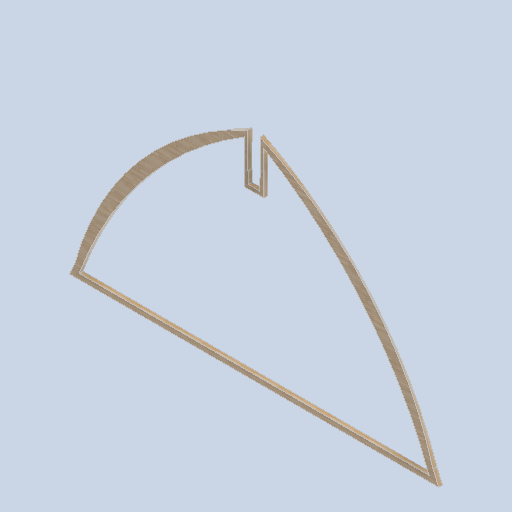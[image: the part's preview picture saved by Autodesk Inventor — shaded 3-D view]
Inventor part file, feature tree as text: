
AUTODESK INVENTOR PART (.ipt)
format: ipt  version: 2024.2 (Build 282272000, 272)  size: 168,448 bytes
history: native  units: in
note: dims shown in document units (in); Inventor stores cm internally (conversion verified against a paired STEP export)
features: other x3, sketch x2, plane x2
ambient origin geometry x8: Origin, YZ Plane, XZ Plane, XY Plane, X Axis, Y Axis, Z Axis, Center Point
bodies: Solid1 (feature_tree)
feature tree (7):
  other  "curve_front_wall_frame.ipt"
  other  "Solid1::curve_front_wall_frame.ipt"
  other  "TaggingFeature1"
  sketch  "Sketch1"  dims[d0=0.3937in]
  sketch  "Sketch4"
  plane  "Work Plane1"
  plane  "Work Plane2"
